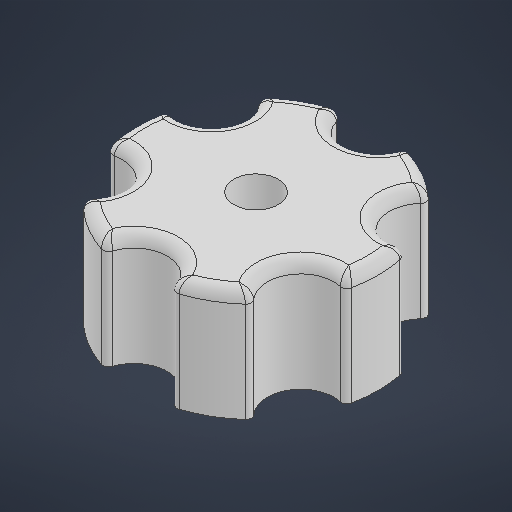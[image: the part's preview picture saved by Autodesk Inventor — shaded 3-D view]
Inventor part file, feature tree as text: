
AUTODESK INVENTOR PART (.ipt)
format: ipt  version: 2025.1 (Build 291241000, 241)  size: 705,024 bytes
history: native  units: mm
features: extrude x2, fillet x2, sketch x2, pattern_circular x1, projected_geometry x1
ambient origin geometry x8: Origin, YZ Plane, XZ Plane, XY Plane, X Axis, Y Axis, Z Axis, Center Point
bodies: Solid1 (feature_tree)
feature tree (8):
  extrude  "Extrusion1"  Depth=22.0mm
  extrude  "Extrusion2"  Depth=6.0mm
  fillet  "Fillet1"  [1 undecoded]
  pattern_circular  "Circular Pattern1"  Count=6 Angle=360.0deg
  fillet  "Fillet2"  Radius=0.5mm
  sketch  "Sketch1"  dims[d0=4.0mm d1=22.0mm]
  sketch  "Sketch2"  dims[d2=10.0mm d3=0.0mm d4=6.0mm d5=0.0mm d6=0.0mm d7=60.0mm d8=360.0deg d10=0.5mm d11=1.0mm]
  projected_geometry  "Projected Loop1"
note: 1 required parameter value undecoded (feature->parameter linkage not recoverable at this tier; creation-order binding heuristic only, values carry confidence <= 0.55)
